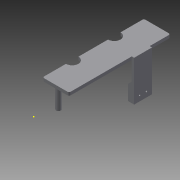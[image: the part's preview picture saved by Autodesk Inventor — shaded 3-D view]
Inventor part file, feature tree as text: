
AUTODESK INVENTOR PART (.ipt)
format: ipt  version: 2015 SP2 (Build 190223200, 223)  size: 197,120 bytes
history: native  units: in
note: dims shown in document units (in); Inventor stores cm internally (conversion verified against a paired STEP export)
features: sketch x19, extrude x9, fillet x1, hole x1
ambient origin geometry x8: Origin, YZ Plane, XZ Plane, XY Plane, X Axis, Y Axis, Z Axis, Center Point
bodies: Body1 (feature_tree)
feature tree (30):
  extrude  "Extrusion4"  Depth=0.6693in
  fillet  "Fillet1"  Radius=0.0787in
  sketch  "Sketch14"  dims[d44=0.0394in d46=0.5315in]
  extrude  "Extrusion8"  Depth=0.0394in
  extrude  "Extrusion9"  Depth=0.1969in TaperAngle=0.0deg
  sketch  "Sketch17"  dims[d52=0.1181in d53=0.5906in d54=0.0in]
  sketch  "Sketch19"  dims[d55=0.1575in d56=0.1575in]
  sketch  "Sketch25"  dims[d57=0.4563in d93=0.0591in d94=0.0in]
  extrude  "Extrusion16"  Depth=0.4698in
  extrude  "Extrusion17"  Depth=0.5906in TaperAngle=0.0deg
  hole  "Hole4"  [1 undecoded]
  sketch  "Sketch30"  dims[d115=0.0394in d116=0.0in]
  sketch  "Sketch31"  dims[d117=0.0394in d118=0.0in]
  sketch  "Sketch35"  dims[d119=0.0197in d120=0.0in]
  sketch  "Sketch36"
  sketch  "Sketch37"
  extrude  "Extrusion21"  Depth=0.0591in TaperAngle=0.0deg
  sketch  "Sketch38"
  sketch  "Sketch39"
  extrude  "Extrusion22"  Depth=0.0394in
  extrude  "Extrusion23"  Depth=0.0787in
  extrude  "Extrusion24"  Depth=0.4527in TaperAngle=0.0deg
  sketch  "Sketch41"
  sketch  "Sketch7"  dims[d16=2.5591in d17=0.6693in d18=0.0787in d19=0.0in]
  sketch  "Sketch15"  dims[d47=0.315in d48=0.1969in d49=0.0in]
  sketch  "Sketch16"  dims[d50=0.6188in d51=0.4698in]
  sketch  "Sketch27"  dims[d95=0.9449in d96=0.0in d97=0.0394in]
  sketch  "Sketch28"  dims[d98=0.0394in d99=0.2362in d100=0.1575in d101=0.0787in d102=90.0deg d103=0.315in d104=0.8108in d111=0.4724in]
  sketch  "Sketch29"  dims[d112=45.0deg d113=0.4527in d114=0.0in]
  sketch  "Sketch40"
note: 1 required parameter value undecoded (feature->parameter linkage not recoverable at this tier; creation-order binding heuristic only, values carry confidence <= 0.55)
